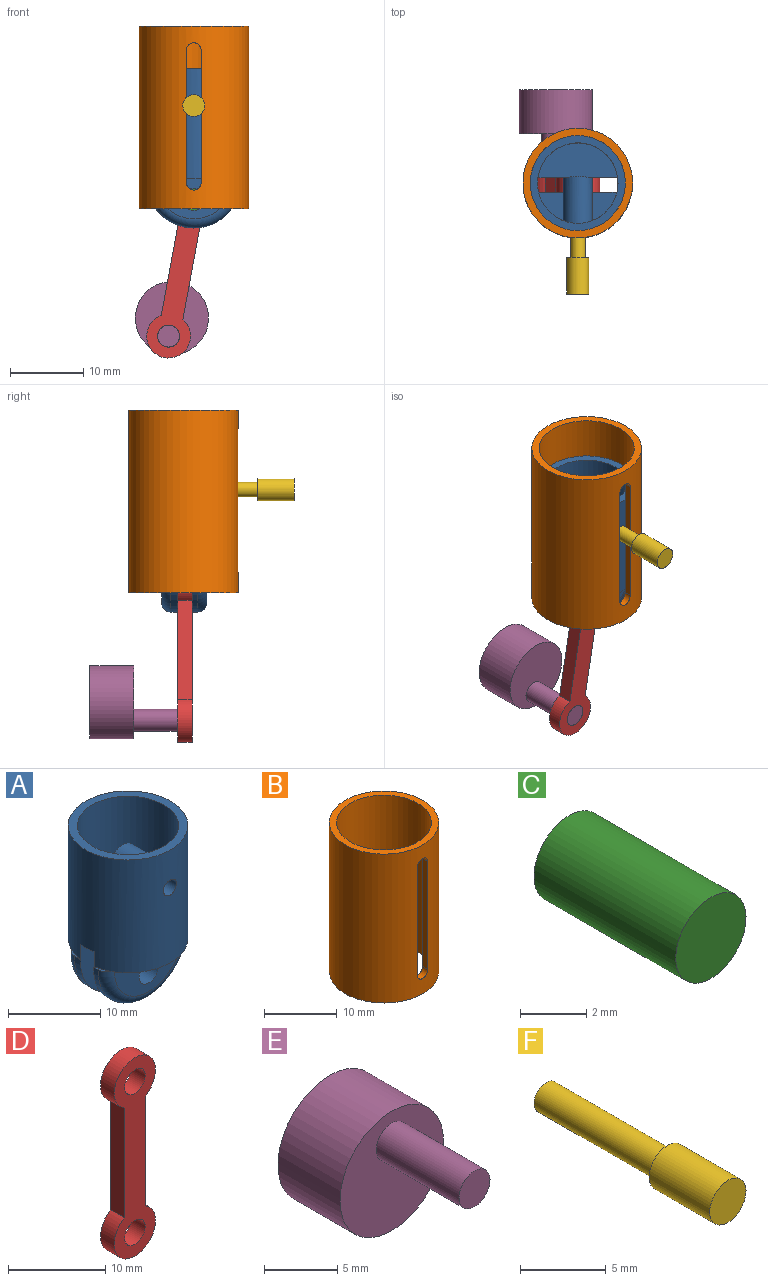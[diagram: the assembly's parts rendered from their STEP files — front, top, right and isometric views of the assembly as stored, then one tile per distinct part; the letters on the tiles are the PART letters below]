
ASSEMBLY  parts=6 mates=6
PART A: 27 faces, bbox 14.1x13x22.3 mm
  f0: plane 10.73x4.29mm, normal (0,0,1), area 34.3mm2, adj f2,f25
  f1: plane 10.89x4.71mm, normal (0,0,1), area 38.8mm2, adj f2,f26
  f2: cylinder r=5.5mm len=14mm, axis (0,0,-1), area 467mm2, adj f0,f1,f3,f10,f14,f17,f25,f26
  f3: plane 2x1.13mm, normal (0,0,-1), area 2mm2, adj f2,f13,f25,f26
  f4: plane 2.02x0.64mm, normal (0,0,1), area 0.4mm2, adj f8,f13,f24,f26
  f5: plane 2.02x0.64mm, normal (0,0,1), area 0.4mm2, adj f8,f13,f24,f26
  f6: plane 1.91x0.8mm, normal (0,0,1), area 0.5mm2, adj f13,f19,f23,f25
  f7: plane 1.9x0.79mm, normal (0,0,1), area 0.5mm2, adj f13,f19,f23,f25
  f8: cylinder r=6.5mm len=13mm, axis (0,-1,0), area 19.3mm2, adj f4,f5,f24,f26
  f9: cylinder r=1.5mm len=3mm, axis (0,-1,0), area 20.5mm2, adj f21,f26
  f10: plane 2x1.13mm, normal (0,0,-1), area 2mm2, adj f2,f13,f25,f26
  f11: plane 11.74x3.71mm, normal (0,0,-1), area 29.3mm2, adj f13,f21,f24
  f12: plane 11.43x3.41mm, normal (0,0,-1), area 26.7mm2, adj f13,f22,f23
  f13: cylinder r=6.5mm len=15mm, axis (0,0,-1), area 601.4mm2, adj f3,f4,f5,f6,f7,f10,f11,f12
  f14: plane 13x13mm, normal (0,0,1), area 37.7mm2, adj f2,f13
  f15: cylinder r=1mm len=6.34mm, axis (0,-1,0), area 39.6mm2, adj f13,f16
  f16: plane 2x2mm, normal (0,-1,0), area 3.1mm2, adj f15
  f17: cylinder r=2mm len=6.34mm, axis (0,-1,0), area 77.4mm2, adj f2,f18
  f18: plane 4x4mm, normal (0,1,0), area 12.6mm2, adj f17
  f19: cylinder r=6.5mm len=13mm, axis (0,-1,0), area 15.2mm2, adj f6,f7,f23,f25
  f20: cylinder r=1.5mm len=3mm, axis (0,-1,0), area 18.7mm2, adj f22,f25
  f21: plane 10.5x5.5mm, normal (0,1,0), area 38.8mm2, adj f9,f11,f24
  f22: plane 10.5x5.5mm, normal (0,-1,0), area 38.8mm2, adj f12,f20,f23
  f23: torus R=5.25mm, axis (0,-1,0), area 38.3mm2, adj f6,f7,f12,f19,f22
  f24: torus R=5.25mm, axis (0,-1,0), area 38.3mm2, adj f4,f5,f8,f11,f21
  f25: plane 13x8.75mm, normal (0,1,0), area 77.3mm2, adj f0,f2,f3,f6,f7,f10,f13,f19
  f26: plane 13x8.75mm, normal (0,-1,0), area 77.4mm2, adj f1,f2,f3,f4,f5,f8,f9,f10
PART B: 8 faces, bbox 15x15x25 mm
  f0: cylinder r=6.5mm len=25mm, axis (0,0,-1), area 981.4mm2, adj f2,f3,f4,f5,f6,f7
  f1: cylinder r=7.5mm len=25mm, axis (0,0,-1), area 1138.6mm2, adj f2,f3,f4,f5,f6,f7
  f2: plane 15x15mm, normal (0,0,1), area 44mm2, adj f0,f1
  f3: plane 15x15mm, normal (0,0,-1), area 44mm2, adj f0,f1
  f4: cylinder r=1mm len=2mm, axis (0,-1,0), area 3.2mm2, adj f0,f1,f5,f7
  f5: plane 18.14x1.01mm, normal (1,0,0), area 18.3mm2, adj f0,f1,f4,f6
  f6: cylinder r=1mm len=2mm, axis (0,-1,0), area 3.2mm2, adj f0,f1,f5,f7
  f7: plane 18.14x1.01mm, normal (-1,0,0), area 18.3mm2, adj f0,f1,f4,f6
PART C: 3 faces, bbox 3x6.1x3 mm
  f0: cylinder r=1.5mm len=6.05mm, axis (0,1,0), area 57.1mm2, adj f1,f2
  f1: plane 3x3mm, normal (0,-1,0), area 7.1mm2, adj f0
  f2: plane 3x3mm, normal (0,1,0), area 7.1mm2, adj f0
PART D: 8 faces, bbox 6x2x25 mm
  f0: cylinder r=3mm len=6mm, axis (0,1,0), area 31.4mm2, adj f1,f4,f5,f6
  f1: plane 13.8x2mm, normal (-1,0,0), area 27.6mm2, adj f0,f2,f5,f6
  f2: cylinder r=3mm len=6mm, axis (0,1,0), area 31.4mm2, adj f1,f4,f5,f6
  f3: cylinder r=1.5mm len=3mm, axis (0,1,0), area 18.8mm2, adj f5,f6
  f4: plane 13.8x2mm, normal (1,0,0), area 27.6mm2, adj f0,f2,f5,f6
  f5: plane 25x6mm, normal (0,-1,0), area 82.2mm2, adj f0,f1,f2,f3,f4,f7
  f6: plane 25x6mm, normal (0,1,0), area 82.2mm2, adj f0,f1,f2,f3,f4,f7
  f7: cylinder r=1.5mm len=3mm, axis (0,1,0), area 18.8mm2, adj f5,f6
PART E: 7 faces, bbox 10x14x10 mm
  f0: cylinder r=5mm len=10mm, axis (0,1,0), area 188.5mm2, adj f1,f2
  f1: plane 10x10mm, normal (0,-1,0), area 71.5mm2, adj f0,f3
  f2: plane 10x10mm, normal (0,1,0), area 75.4mm2, adj f0,f5
  f3: cylinder r=1.5mm len=8mm, axis (0,1,0), area 75.4mm2, adj f1,f4
  f4: plane 3x3mm, normal (0,-1,0), area 7.1mm2, adj f3
  f5: cylinder r=1mm len=3mm, axis (0,1,0), area 18.8mm2, adj f2,f6
  f6: plane 2x2mm, normal (0,1,0), area 3.1mm2, adj f5
PART F: 5 faces, bbox 3x15x3 mm
  f0: cylinder r=1.5mm len=5mm, axis (0,1,0), area 47.1mm2, adj f1,f2
  f1: plane 3x3mm, normal (0,-1,0), area 7.1mm2, adj f0
  f2: plane 3x3mm, normal (0,1,0), area 3.9mm2, adj f0,f3
  f3: cylinder r=1mm len=10mm, axis (0,-1,0), area 62.8mm2, adj f2,f4
  f4: plane 2x2mm, normal (0,1,0), area 3.1mm2, adj f3
PLACE A t=(-5.43,10.73,34.27)mm
PLACE B t=(-5.43,-0.34,30.15)mm fixed
PLACE C t=(-5.43,23.75,21.08)mm
PLACE D rot(axis=(0,1,0),10.4deg) t=(-9.99,21.67,6.67)mm
PLACE E rot(axis=(0,-1,0),169.6deg) t=(-8.42,33.67,15.21)mm
PLACE F t=(-5.43,10.73,34.73)mm
MATE revolute A.f9 <-> D.f3  axis (0,1,0) through (-5.43,19.67,31.44)mm
MATE cylindrical C.f0 <-> A.f9  axis (0,-1,0) through (-5.43,17.69,31.44)mm
MATE slider A.f2 <-> B.f0  axis (0,0,-1) through (-5.43,20.88,49.27)mm
MATE revolute C.f0 <-> A.f9  axis (0,-1,0) through (-5.43,17.69,31.44)mm
MATE revolute E.f3 <-> D.f2  axis (0,-1,0) through (-8.87,19.67,12.75)mm
MATE fastened F.f0 <-> A.f15  axis (0,1,0) through (-5.43,20.73,44.27)mm
